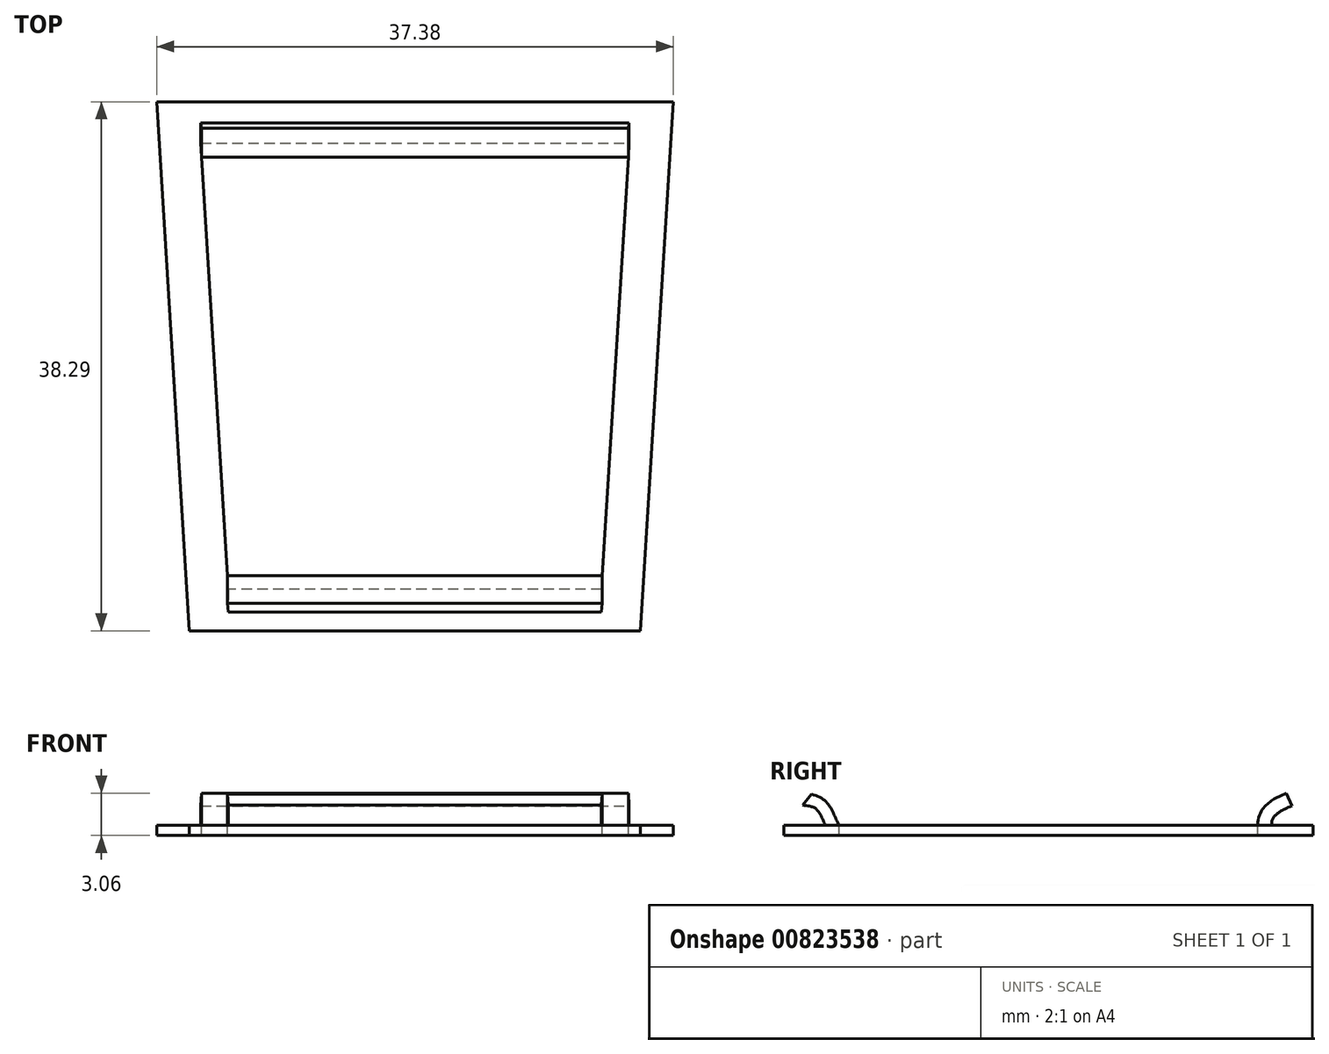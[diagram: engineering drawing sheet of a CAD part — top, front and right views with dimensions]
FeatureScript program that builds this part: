
annotation { "Feature Type Name" : "Feature", "Feature Type Description" : "" }
export const myFeature = defineFeature(function(context is Context, id is Id, definition is map)
    precondition{}
    {
        {
            var Q0;
            Q0=qCreatedBy(makeId("Top.planeOp"),FACE);
            var sketch = newSketch(context, id + "F0", { "sketchPlane" : qUnion([Q0])});
            skLineSegment(sketch, "E0", {"start": v(0, 13.03) * mm, "end": v(15.5, 13.03) * mm});
            skLineSegment(sketch, "E1", {"start": v(15.5, 13.03) * mm, "end": v(13.5, -19.26) * mm});
            skLineSegment(sketch, "E2", {"start": v(13.5, -19.26) * mm, "end": v(0, -19.26) * mm});
            skLineSegment(sketch, "E3", {"start": v(0, -19.26) * mm, "end": v(-13.5, -19.26) * mm});
            skLineSegment(sketch, "E4", {"start": v(-13.5, -19.26) * mm, "end": v(-15.5, 13.03) * mm});
            skLineSegment(sketch, "E5", {"start": v(-15.5, 13.03) * mm, "end": v(0, 13.03) * mm});
            skLineSegment(sketch, "E6", {"start": v(15.5, 13.03) * mm, "end": v(18.5, 13.03) * mm});
            skLineSegment(sketch, "E7", {"start": v(18.5, 13.03) * mm, "end": v(16.5, -19.26) * mm});
            skLineSegment(sketch, "E8", {"start": v(16.5, -19.26) * mm, "end": v(13.5, -19.26) * mm});
            skLineSegment(sketch, "E9", {"start": v(-15.5, 13.03) * mm, "end": v(-18.5, 13.03) * mm});
            skLineSegment(sketch, "E10", {"start": v(-18.5, 13.03) * mm, "end": v(-16.5, -19.26) * mm});
            skLineSegment(sketch, "E11", {"start": v(-16.5, -19.26) * mm, "end": v(-13.5, -19.26) * mm});
            skLineSegment(sketch, "E12", {"start": v(-18.5, 13.03) * mm, "end": v(-18.69, 16.03) * mm});
            skLineSegment(sketch, "E13", {"start": v(-18.69, 16.03) * mm, "end": v(18.69, 16.03) * mm});
            skLineSegment(sketch, "E14", {"start": v(18.69, 16.03) * mm, "end": v(18.5, 13.03) * mm});
            skLineSegment(sketch, "E15", {"start": v(-16.5, -19.26) * mm, "end": v(-16.31, -22.26) * mm});
            skLineSegment(sketch, "E16", {"start": v(-16.31, -22.26) * mm, "end": v(16.31, -22.26) * mm});
            skLineSegment(sketch, "E17", {"start": v(16.31, -22.26) * mm, "end": v(16.5, -19.26) * mm});
            skLineSegment(sketch, "E18", {"start": v(-15.44, 12.03) * mm, "end": v(15.44, 12.03) * mm});
            skLineSegment(sketch, "E19", {"start": v(-13.56, -18.27) * mm, "end": v(13.56, -18.27) * mm});
            skSolve(sketch);
        }
        {
            var Q0;
            Q0=qCreatedBy(makeId("Right.planeOp"),FACE);
            var sketch = newSketch(context, id + "F1", { "sketchPlane" : qUnion([Q0])});
            skFitSpline(sketch, "E20", {"points": [v(12.51, 0) * mm, v(13.06, 1.18) * mm, v(14.3, 1.87) * mm], "startDerivative": vector(0, 3.6) * mm, "endDerivative": vector(3.39, 1.5) * mm});
            skFitSpline(sketch, "E21", {"points": [v(-18.7, 0) * mm, v(-19.34, 1.24) * mm, v(-20.54, 1.89) * mm], "startDerivative": vector(-1.13, 2.21) * mm, "endDerivative": vector(-3.66, 0.73) * mm});
            skSolve(sketch);
        }
        {
            var Q0;
            {var subQ4=sQuery(id+"F0.wireOp",EDGE,"E0");Q0=makeQuery(id+"F0.imprint","IMPRINT",FACE,{"disambiguationData":[TD([[makeQuery(id+"F0.imprint","IMPRINT",EDGE,{"derivedFrom":subQ4}),-1.0]])]});}
            var Q1;
            Q1=sQuery(id+"F1.wireOp",EDGE,"E20");
            sweep(context, id + "F2", {"profiles" : qUnion([Q0]), "path" : qUnion([Q1])});
        }
        {
            var Q0;
            {var subQ3=sQuery(id+"F0.wireOp",EDGE,"E2");Q0=makeQuery(id+"F0.imprint","IMPRINT",FACE,{"disambiguationData":[TD([[makeQuery(id+"F0.imprint","IMPRINT",EDGE,{"derivedFrom":subQ3}),-1.0]])]});}
            var Q1;
            Q1=sQuery(id+"F1.wireOp",EDGE,"E21");
            sweep(context, id + "F3", {"profiles" : qUnion([Q0]), "path" : qUnion([Q1])});
        }
        {
            var Q0;
            Q0=makeQuery(id+"F0.imprint","IMPRINT",FACE,{"disambiguationData":[TD([[makeQuery(id+"F0.imprint","IMPRINT",EDGE,{"derivedFrom":sQuery(id+"F0.wireOp",EDGE,"E0")}),1.0]])]});
            var Q1;
            {var subQ0=sQuery(id+"F0.wireOp",EDGE,"E9");Q1=makeQuery(id+"F0.imprint","IMPRINT",FACE,{"disambiguationData":[TD([[makeQuery(id+"F0.imprint","IMPRINT",EDGE,{"derivedFrom":subQ0}),1.0]])]});}
            var Q2;
            {var subQ0=sQuery(id+"F0.wireOp",EDGE,"E6");Q2=makeQuery(id+"F0.imprint","IMPRINT",FACE,{"disambiguationData":[TD([[makeQuery(id+"F0.imprint","IMPRINT",EDGE,{"derivedFrom":subQ0}),-1.0]])]});}
            var Q3;
            Q3=makeQuery(id+"F0.imprint","IMPRINT",FACE,{"disambiguationData":[TD([[makeQuery(id+"F0.imprint","IMPRINT",EDGE,{"derivedFrom":sQuery(id+"F0.wireOp",EDGE,"E2")}),1.0]])]});
            var Q4;
            {var subQ3=sQuery(id+"F0.wireOp",EDGE,"E2");Q4=makeQuery(id+"F0.imprint","IMPRINT",FACE,{"disambiguationData":[TD([[makeQuery(id+"F0.imprint","IMPRINT",EDGE,{"derivedFrom":subQ3}),-1.0]])]});}
            var Q5;
            {var subQ4=sQuery(id+"F0.wireOp",EDGE,"E0");Q5=makeQuery(id+"F0.imprint","IMPRINT",FACE,{"disambiguationData":[TD([[makeQuery(id+"F0.imprint","IMPRINT",EDGE,{"derivedFrom":subQ4}),-1.0]])]});}
            extrude(context, id + "F4", {"entities" : qUnion([Q0, Q1, Q2, Q3, Q4, Q5]), "operationType" : NewBodyOperationType.ADD, "oppositeDirection" : true, "depth" : .75 * mm, "offsetDistance" : 25 * mm});
        }
    });
